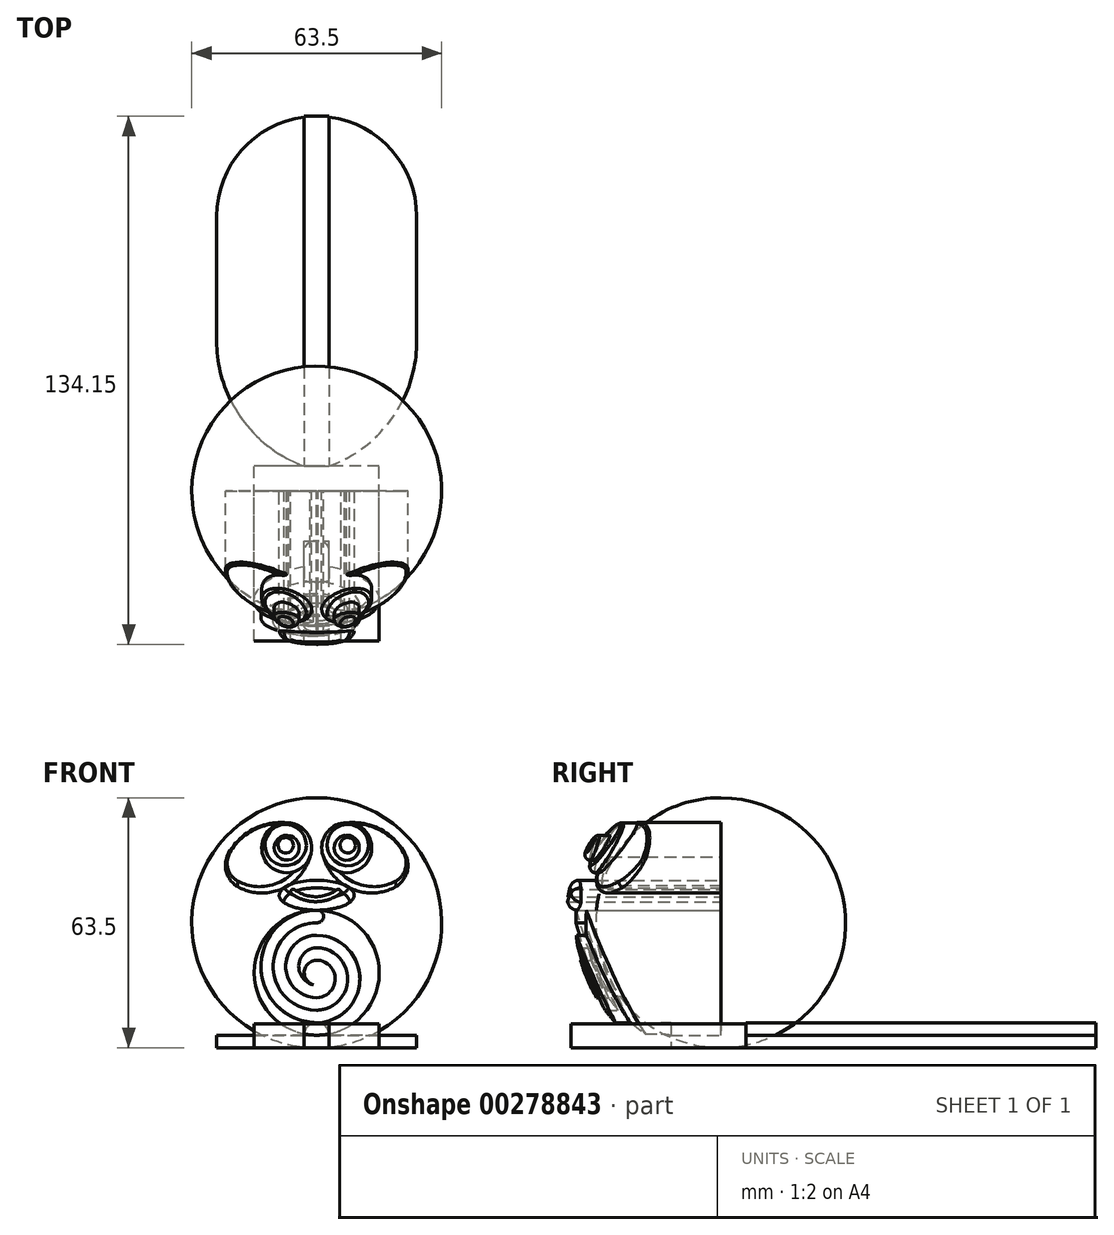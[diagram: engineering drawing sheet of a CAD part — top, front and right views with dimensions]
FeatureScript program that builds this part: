
annotation { "Feature Type Name" : "Feature", "Feature Type Description" : "" }
export const myFeature = defineFeature(function(context is Context, id is Id, definition is map)
    precondition{}
    {
        {
            var Q0;
            Q0=qCreatedBy(makeId("Front.planeOp"),FACE);
            var sketch = newSketch(context, id + "F0", { "sketchPlane" : qUnion([Q0])});
            skArc(sketch, "E0", {"start": v(-7.62, 57.15) * mm, "mid": v(-12.11, 46.3) * mm, "end": v(-1.27, 50.8) * mm});
            skCircle(sketch, "E1", {"center": v(0, 19.05) * mm, "radius": 15.88 * mm});
            skLineSegment(sketch, "E2", {"start": v(-7.62, 50.8) * mm, "end": v(-7.62, 57.15) * mm, "construction": true});
            skArc(sketch, "E3", {"start": v(-7.62, 57.15) * mm, "mid": v(-16.13, 55.5) * mm, "end": v(-22.36, 49.48) * mm});
            skArc(sketch, "E4", {"start": v(-19.75, 40.71) * mm, "mid": v(-7.83, 40.85) * mm, "end": v(-1.27, 50.8) * mm});
            skPoint(sketch, "E5.visualSharp", {"position": v(-24.13, 44.45) * mm});
            skArc(sketch, "E5.filletArc", {"start": v(-22.36, 49.48) * mm, "mid": v(-22.92, 44.54) * mm, "end": v(-19.75, 40.71) * mm});
            skPoint(sketch, "E6.center.orphan", {"position": v(7.62, 50.8) * mm});
            skArc(sketch, "E7.MirrorCS", {"start": v(7.62, 57.15) * mm, "mid": v(12.11, 46.3) * mm, "end": v(1.27, 50.8) * mm});
            skArc(sketch, "E8.MirrorCS", {"start": v(19.75, 40.71) * mm, "mid": v(7.83, 40.85) * mm, "end": v(1.27, 50.8) * mm});
            skArc(sketch, "E9.MirrorCS", {"start": v(22.36, 49.48) * mm, "mid": v(22.92, 44.54) * mm, "end": v(19.75, 40.71) * mm});
            skArc(sketch, "E10.MirrorCS", {"start": v(7.62, 57.15) * mm, "mid": v(16.13, 55.5) * mm, "end": v(22.36, 49.48) * mm});
            skSolve(sketch);
        }
        {
            var Q0;
            Q0 = qSketchRegion(id + "F0", true);
            extrude(context, id + "F1", {"entities" : qUnion([Q0]), "depth" : 50.8 * mm});
        }
        {
            var Q0;
            Q0=qCreatedBy(makeId("Front.planeOp"),FACE);
            var sketch = newSketch(context, id + "F2", { "sketchPlane" : qUnion([Q0])});
            skLineSegment(sketch, "E11", {"start": v(0, 0) * mm, "end": v(0, 63.5) * mm});
            skArc(sketch, "E12", {"start": v(0, 0) * mm, "mid": v(31.75, 31.75) * mm, "end": v(0, 63.5) * mm});
            skSolve(sketch);
        }
        {
            var Q0;
            Q0=qCreatedBy(makeId("Front.planeOp"),FACE);
            var sketch = newSketch(context, id + "F3", { "sketchPlane" : qUnion([Q0])});
            skCircle(sketch, "E13", {"center": v(0, 19.05) * mm, "radius": 12.7 * mm, "construction": true});
            skCircle(sketch, "E14", {"center": v(0, 19.05) * mm, "radius": 15.88 * mm, "construction": true});
            skCircle(sketch, "E15", {"center": v(0, 19.05) * mm, "radius": 9.53 * mm, "construction": true});
            skCircle(sketch, "E16", {"center": v(0, 19.05) * mm, "radius": 6.35 * mm, "construction": true});
            skArc(sketch, "E17", {"start": v(0.3, 22.21) * mm, "mid": v(-3.17, 19.2) * mm, "end": v(0, 15.88) * mm});
            skLineSegment(sketch, "E18", {"start": v(0, 9.53) * mm, "end": v(0, 12.7) * mm, "construction": true});
            skLineSegment(sketch, "E19", {"start": v(15.88, 19.05) * mm, "end": v(-15.88, 19.05) * mm, "construction": true});
            skArc(sketch, "E20", {"start": v(0, 34.92) * mm, "mid": v(-14.19, 20.64) * mm, "end": v(0, 6.35) * mm});
            skLineSegment(sketch, "E21", {"start": v(0, 6.35) * mm, "end": v(0, 3.18) * mm, "construction": true});
            skArc(sketch, "E22", {"start": v(0, 3.17) * mm, "mid": v(14.26, 17.46) * mm, "end": v(0, 31.75) * mm});
            skLineSegment(sketch, "E23.trimOffspring", {"start": v(0, 31.75) * mm, "end": v(0, 34.93) * mm, "construction": true});
            skLineSegment(sketch, "E24.trimOffspring", {"start": v(0, 15.88) * mm, "end": v(0, 22.23) * mm, "construction": true});
            skLineSegment(sketch, "E25.trimOffspring", {"start": v(0, 25.4) * mm, "end": v(0, 28.58) * mm, "construction": true});
            skArc(sketch, "E26", {"start": v(0, 31.75) * mm, "mid": v(-11.08, 20.64) * mm, "end": v(0, 9.53) * mm});
            skArc(sketch, "E27", {"start": v(0, 6.35) * mm, "mid": v(10.96, 17.46) * mm, "end": v(0, 28.58) * mm});
            skArc(sketch, "E28", {"start": v(0, 28.58) * mm, "mid": v(-7.87, 20.64) * mm, "end": v(0, 12.7) * mm});
            skArc(sketch, "E29", {"start": v(0, 9.53) * mm, "mid": v(7.84, 17.46) * mm, "end": v(0, 25.4) * mm});
            skArc(sketch, "E30", {"start": v(0, 12.7) * mm, "mid": v(4.7, 17.46) * mm, "end": v(0, 22.23) * mm});
            skArc(sketch, "E31", {"start": v(0, 25.4) * mm, "mid": v(-4.57, 20.64) * mm, "end": v(0, 15.88) * mm});
            skArc(sketch, "E32", {"start": v(0, 31.75) * mm, "mid": v(1.75, 33.34) * mm, "end": v(0, 34.93) * mm});
            skArc(sketch, "E33", {"start": v(0, 6.35) * mm, "mid": v(-0.24, 6.37) * mm, "end": v(-0.48, 6.36) * mm});
            skArc(sketch, "E34.trimOffspring", {"start": v(-0.6, 3.19) * mm, "mid": v(-0.3, 3.15) * mm, "end": v(0, 3.18) * mm});
            skCircle(sketch, "E35", {"center": v(-7.62, 50.8) * mm, "radius": 6.35 * mm});
            skCircle(sketch, "E36", {"center": v(7.62, 50.8) * mm, "radius": 6.35 * mm});
            skSolve(sketch);
        }
        {
            var Q0;
            Q0=qCreatedBy(makeId("Front.planeOp"),FACE);
            var sketch = newSketch(context, id + "F4", { "sketchPlane" : qUnion([Q0])});
            skLineSegment(sketch, "E37.bottom", {"start": v(-15.88, 0) * mm, "end": v(15.87, 0) * mm});
            skLineSegment(sketch, "E37.top", {"start": v(-15.88, 6.03) * mm, "end": v(15.87, 6.03) * mm});
            skLineSegment(sketch, "E37.left", {"start": v(-15.88, 0) * mm, "end": v(-15.88, 6.03) * mm});
            skLineSegment(sketch, "E37.right", {"start": v(15.87, 0) * mm, "end": v(15.87, 6.03) * mm});
            skSolve(sketch);
        }
        {
            var Q0;
            Q0=qCreatedBy(makeId("Front.planeOp"),FACE);
            var sketch = newSketch(context, id + "F5", { "sketchPlane" : qUnion([Q0])});
            skPoint(sketch, "E38.orphan", {"position": v(0, 4.54) * mm});
            skLineSegment(sketch, "E39", {"start": v(0, 141) * mm, "end": v(0, 66.04) * mm});
            skPoint(sketch, "E40.orphan", {"position": v(0, 72.33) * mm});
            skArc(sketch, "E41", {"start": v(0, -77.5) * mm, "mid": v(109.26, 31.75) * mm, "end": v(0, 141) * mm});
            skArc(sketch, "E42", {"start": v(0, -2.54) * mm, "mid": v(34.3, 31.75) * mm, "end": v(0, 66.04) * mm});
            skLineSegment(sketch, "E43", {"start": v(0, -77.5) * mm, "end": v(0, -2.54) * mm});
            skSolve(sketch);
        }
        {
            var Q0;
            Q0=makeQuery(id+"F5.imprint","IMPRINT",FACE,{"disambiguationData":[TD([[makeQuery(id+"F5.imprint","IMPRINT",EDGE,{"derivedFrom":sQuery(id+"F5.wireOp",EDGE,"E39")}),1.0]])]});
            var Q1;
            Q1=sQuery(id+"F5.wireOp",EDGE,"E39");
            revolve(context, id + "F6", {"operationType" : NewBodyOperationType.REMOVE, "entities" : qUnion([Q0]), "axis" : qUnion([Q1]), "revolveType" : RevolveType.FULL, "oppositeDirection" : true});
        }
        {
            var Q0;
            Q0 = qSketchRegion(id + "F3", true);
            extrude(context, id + "F7", {"entities" : qUnion([Q0]), "operationType" : NewBodyOperationType.ADD, "depth" : 63.5 * mm});
        }
        {
            var Q0;
            Q0=qCreatedBy(makeId("Front.planeOp"),FACE);
            var sketch = newSketch(context, id + "F8", { "sketchPlane" : qUnion([Q0])});
            skArc(sketch, "E44", {"start": v(0, -5.08) * mm, "mid": v(36.83, 31.75) * mm, "end": v(0, 68.58) * mm});
            skArc(sketch, "E45", {"start": v(0, -69.85) * mm, "mid": v(101.6, 31.75) * mm, "end": v(0, 133.35) * mm});
            skLineSegment(sketch, "E46", {"start": v(0, -5.08) * mm, "end": v(0, -69.85) * mm});
            skLineSegment(sketch, "E47", {"start": v(0, 68.58) * mm, "end": v(0, 133.35) * mm});
            skSolve(sketch);
        }
        {
            var Q0;
            Q0 = qSketchRegion(id + "F8", true);
            var Q1;
            Q1=sQuery(id+"F8.wireOp",EDGE,"E47");
            revolve(context, id + "F9", {"operationType" : NewBodyOperationType.REMOVE, "entities" : qUnion([Q0]), "axis" : qUnion([Q1]), "revolveType" : RevolveType.FULL, "oppositeDirection" : true});
        }
        {
            var Q0;
            Q0=qCreatedBy(makeId("Front.planeOp"),FACE);
            var sketch = newSketch(context, id + "F10", { "sketchPlane" : qUnion([Q0])});
            skEllipse(sketch, "E48", {"center": v(0, 38.73) * mm, "majorRadius": 9.53 * mm, "minorRadius": 3.81 * mm, "majorAxis": v(1, 0)});
            skArc(sketch, "E49", {"start": v(-5.61, 40.13) * mm, "mid": v(-0.25, 38.36) * mm, "end": v(5.1, 40.13) * mm});
            skArc(sketch, "E50.0", {"start": v(-6.37, 39.11) * mm, "mid": v(-0.25, 37.1) * mm, "end": v(5.86, 39.11) * mm});
            skArc(sketch, "E51", {"start": v(-5.61, 40.13) * mm, "mid": v(-6.5, 40) * mm, "end": v(-6.37, 39.11) * mm});
            skArc(sketch, "E52", {"start": v(5.86, 39.11) * mm, "mid": v(6, 40) * mm, "end": v(5.1, 40.13) * mm});
            skCircle(sketch, "E53", {"center": v(-7.62, 50.8) * mm, "radius": 3.18 * mm});
            skCircle(sketch, "E54", {"center": v(7.62, 50.8) * mm, "radius": 3.18 * mm});
            skSolve(sketch);
        }
        {
            var Q0;
            Q0 = qSketchRegion(id + "F10", true);
            extrude(context, id + "F11", {"entities" : qUnion([Q0]), "operationType" : NewBodyOperationType.ADD, "depth" : 76.2 * mm});
        }
        {
            var Q0;
            Q0=qCreatedBy(makeId("Front.planeOp"),FACE);
            var sketch = newSketch(context, id + "F12", { "sketchPlane" : qUnion([Q0])});
            skArc(sketch, "E55", {"start": v(0, -7.62) * mm, "mid": v(39.37, 31.75) * mm, "end": v(0, 71.12) * mm});
            skArc(sketch, "E56", {"start": v(0, -69.85) * mm, "mid": v(101.6, 31.75) * mm, "end": v(0, 133.35) * mm});
            skLineSegment(sketch, "E57", {"start": v(0, -7.62) * mm, "end": v(0, -69.85) * mm});
            skLineSegment(sketch, "E58", {"start": v(0, 71.12) * mm, "end": v(0, 133.35) * mm});
            skSolve(sketch);
        }
        {
            var Q0;
            Q0 = qSketchRegion(id + "F12", true);
            var Q1;
            Q1=sQuery(id+"F12.wireOp",EDGE,"E58");
            revolve(context, id + "F13", {"operationType" : NewBodyOperationType.REMOVE, "entities" : qUnion([Q0]), "axis" : qUnion([Q1]), "revolveType" : RevolveType.FULL, "oppositeDirection" : true});
        }
        {
            var Q0;
            Q0 = qSketchRegion(id + "F4", true);
            extrude(context, id + "F14", {"entities" : qUnion([Q0]), "endBound" : BoundingType.SYMMETRIC, "depth" : 76.2 * mm});
        }
        {
            var Q0;
            Q0=makeQuery(id+"F14.opExtrude","SWEPT_FACE",FACE,{"disambiguationData":[OSD([sQuery(id+"F4.wireOp",EDGE,"E37.bottom")])]});
            var sketch = newSketch(context, id + "F15", { "sketchPlane" : qUnion([Q0])});
            skLineSegment(sketch, "E59.bottom", {"start": v(-15.88, -6.35) * mm, "end": v(15.87, -6.35) * mm});
            skLineSegment(sketch, "E59.top", {"start": v(-15.88, -38.1) * mm, "end": v(15.87, -38.1) * mm});
            skLineSegment(sketch, "E59.left", {"start": v(-15.88, -6.35) * mm, "end": v(-15.88, -38.1) * mm});
            skLineSegment(sketch, "E59.right", {"start": v(15.87, -6.35) * mm, "end": v(15.87, -38.1) * mm});
            skLineSegment(sketch, "E60.bottom", {"start": v(-3.18, 38.1) * mm, "end": v(3.17, 38.1) * mm});
            skLineSegment(sketch, "E60.top", {"start": v(-3.17, 12.7) * mm, "end": v(3.18, 12.7) * mm});
            skLineSegment(sketch, "E60.left", {"start": v(-3.18, 38.1) * mm, "end": v(-3.17, 12.7) * mm});
            skLineSegment(sketch, "E60.right", {"start": v(3.17, 38.1) * mm, "end": v(3.18, 12.7) * mm});
            skSolve(sketch);
        }
        {
            var Q0;
            Q0 = qSketchRegion(id + "F15", true);
            extrude(context, id + "F16", {"entities" : qUnion([Q0]), "operationType" : NewBodyOperationType.REMOVE, "oppositeDirection" : true, "depth" : 6.35 * mm});
        }
        {
            var Q0;
            Q0=makeQuery(id+"F14.opExtrude","SWEPT_EDGE",EDGE,{"disambiguationData":[OSD([sQuery(id+"F4.wireOp",EDGE,"E37.top"),sQuery(id+"F4.wireOp",EDGE,"E37.right")])]});
            var Q1;
            {var subQ0=sQuery(id+"F4.wireOp",EDGE,"E37.right");var subQ1=sQuery(id+"F4.wireOp",EDGE,"E37.top");Q1=makeQuery(id+"F16.boolean.opBoolean","SPLIT",EDGE,{"disambiguationData":[TD([makeQuery(id+"F14.opExtrude","SWEPT_FACE",FACE,{"disambiguationData":[OSD([subQ0])]})])],"derivedFrom":makeQuery(id+"F14.opExtrude","CAP_EDGE",EDGE,{"disambiguationData":[OSD([subQ1])],"isStart":false})});}
            var Q2;
            Q2=makeQuery(id+"F14.opExtrude","CAP_EDGE",EDGE,{"disambiguationData":[OSD([sQuery(id+"F4.wireOp",EDGE,"E37.right")])],"isStart":false});
            var Q3;
            Q3=makeQuery(id+"F16.boolean.opBoolean","COPY",EDGE,{"derivedFrom":makeQuery(id+"F16.opExtrude","SWEPT_EDGE",EDGE,{"disambiguationData":[OSD([sQuery(id+"F4.wireOp",EDGE,"E37.bottom"),sQuery(id+"F15.wireOp",EDGE,"E60.bottom"),sQuery(id+"F15.wireOp",EDGE,"E60.right")])]})});
            var Q4;
            Q4=makeQuery(id+"F16.boolean.opBoolean","INTERSECT",EDGE,{"derivedFrom":[makeQuery(id+"F14.opExtrude","SWEPT_FACE",FACE,{"disambiguationData":[OSD([sQuery(id+"F4.wireOp",EDGE,"E37.top")])]}),makeQuery(id+"F16.opExtrude","SWEPT_FACE",FACE,{"disambiguationData":[OSD([sQuery(id+"F15.wireOp",EDGE,"E60.right")])]})]});
            var Q5;
            {var subQ0=sQuery(id+"F4.wireOp",EDGE,"E37.left");var subQ1=sQuery(id+"F4.wireOp",EDGE,"E37.top");Q5=makeQuery(id+"F16.boolean.opBoolean","SPLIT",EDGE,{"disambiguationData":[TD([makeQuery(id+"F14.opExtrude","SWEPT_FACE",FACE,{"disambiguationData":[OSD([subQ0])]})])],"derivedFrom":makeQuery(id+"F14.opExtrude","CAP_EDGE",EDGE,{"disambiguationData":[OSD([subQ1])],"isStart":false})});}
            var Q6;
            Q6=makeQuery(id+"F16.boolean.opBoolean","INTERSECT",EDGE,{"derivedFrom":[makeQuery(id+"F14.opExtrude","SWEPT_FACE",FACE,{"disambiguationData":[OSD([sQuery(id+"F4.wireOp",EDGE,"E37.top")])]}),makeQuery(id+"F16.opExtrude","SWEPT_FACE",FACE,{"disambiguationData":[OSD([sQuery(id+"F15.wireOp",EDGE,"E60.left")])]})]});
            var Q7;
            Q7=makeQuery(id+"F16.boolean.opBoolean","COPY",EDGE,{"derivedFrom":makeQuery(id+"F16.opExtrude","SWEPT_EDGE",EDGE,{"disambiguationData":[OSD([sQuery(id+"F15.wireOp",EDGE,"E60.top"),sQuery(id+"F15.wireOp",EDGE,"E60.left")])]})});
            var Q8;
            Q8=makeQuery(id+"F16.boolean.opBoolean","COPY",EDGE,{"derivedFrom":makeQuery(id+"F16.opExtrude","SWEPT_EDGE",EDGE,{"disambiguationData":[OSD([sQuery(id+"F15.wireOp",EDGE,"E60.top"),sQuery(id+"F15.wireOp",EDGE,"E60.right")])]})});
            var Q9;
            Q9=makeQuery(id+"F14.opExtrude","CAP_EDGE",EDGE,{"disambiguationData":[OSD([sQuery(id+"F4.wireOp",EDGE,"E37.left")])],"isStart":false});
            var Q10;
            Q10=makeQuery(id+"F14.opExtrude","SWEPT_EDGE",EDGE,{"disambiguationData":[OSD([sQuery(id+"F4.wireOp",EDGE,"E37.top"),sQuery(id+"F4.wireOp",EDGE,"E37.left")])]});
            var Q11;
            Q11=makeQuery(id+"F16.boolean.opBoolean","COPY",EDGE,{"derivedFrom":makeQuery(id+"F16.opExtrude","SWEPT_EDGE",EDGE,{"disambiguationData":[OSD([sQuery(id+"F4.wireOp",EDGE,"E37.bottom"),sQuery(id+"F4.wireOp",EDGE,"E37.left"),sQuery(id+"F15.wireOp",EDGE,"E59.bottom"),sQuery(id+"F15.wireOp",EDGE,"E59.left")])]})});
            var Q12;
            Q12=makeQuery(id+"F16.boolean.opBoolean","COPY",EDGE,{"derivedFrom":makeQuery(id+"F16.opExtrude","SWEPT_EDGE",EDGE,{"disambiguationData":[OSD([sQuery(id+"F4.wireOp",EDGE,"E37.bottom"),sQuery(id+"F4.wireOp",EDGE,"E37.right"),sQuery(id+"F15.wireOp",EDGE,"E59.bottom"),sQuery(id+"F15.wireOp",EDGE,"E59.right")])]})});
            fillet(context, id + "F17", {"entities" : qUnion([Q0, Q1, Q2, Q3, Q4, Q5, Q6, Q7, Q8, Q9, Q10, Q11, Q12]), "radius" : 2.54 * mm, "tangentPropagation" : true, "allowEdgeOverflow" : false});
        }
        {
            var Q0;
            Q0=makeQuery(id+"F16.boolean.opBoolean","COPY",FACE,{"derivedFrom":makeQuery(id+"F16.opExtrude","SWEPT_FACE",FACE,{"disambiguationData":[OSD([sQuery(id+"F15.wireOp",EDGE,"E59.bottom")])]})});
            var sketch = newSketch(context, id + "F18", { "sketchPlane" : qUnion([Q0])});
            skLineSegment(sketch, "E61.bottom", {"start": v(-25.4, 0) * mm, "end": v(25.4, 0) * mm});
            skLineSegment(sketch, "E61.top", {"start": v(-25.4, 3.18) * mm, "end": v(-3.18, 3.18) * mm});
            skLineSegment(sketch, "E61.left", {"start": v(-25.4, 0) * mm, "end": v(-25.4, 3.17) * mm});
            skLineSegment(sketch, "E61.right", {"start": v(25.4, 0) * mm, "end": v(25.4, 3.18) * mm});
            skArc(sketch, "E62", {"start": v(3.18, 3.18) * mm, "mid": v(0, 6.35) * mm, "end": v(-3.17, 3.18) * mm});
            skLineSegment(sketch, "E63.trimOffspring", {"start": v(3.17, 3.18) * mm, "end": v(25.4, 3.18) * mm});
            skSolve(sketch);
        }
        {
            var Q0;
            Q0 = qSketchRegion(id + "F18", true);
            extrude(context, id + "F19", {"entities" : qUnion([Q0]), "operationType" : NewBodyOperationType.ADD, "depth" : 88.9 * mm});
        }
        {
            var Q0;
            Q0=makeQuery(id+"F19.opExtrude","SWEPT_FACE",FACE,{"disambiguationData":[OSD([sQuery(id+"F18.wireOp",EDGE,"E63.trimOffspring")])]});
            var sketch = newSketch(context, id + "F20", { "sketchPlane" : qUnion([Q0])});
            skLineSegment(sketch, "E64", {"start": v(-25.4, 38.1) * mm, "end": v(-25.4, 69.85) * mm});
            skLineSegment(sketch, "E65", {"start": v(25.4, 69.85) * mm, "end": v(25.4, 38.1) * mm});
            skArc(sketch, "E66", {"start": v(25.4, 69.85) * mm, "mid": v(0, 95.25) * mm, "end": v(-25.4, 69.85) * mm});
            skArc(sketch, "E67", {"start": v(-25.4, 38.1) * mm, "mid": v(-19.3, 18.72) * mm, "end": v(-3.17, 6.35) * mm});
            skArc(sketch, "E68", {"start": v(3.18, 6.35) * mm, "mid": v(19.3, 18.72) * mm, "end": v(25.4, 38.1) * mm});
            skLineSegment(sketch, "E69", {"start": v(-3.17, 6.35) * mm, "end": v(-41.55, 6.35) * mm});
            skLineSegment(sketch, "E70", {"start": v(-41.55, 6.35) * mm, "end": v(-41.55, 107.73) * mm});
            skLineSegment(sketch, "E71", {"start": v(-41.55, 107.73) * mm, "end": v(64.16, 107.73) * mm});
            skLineSegment(sketch, "E72", {"start": v(64.16, 107.73) * mm, "end": v(64.16, 6.35) * mm});
            skLineSegment(sketch, "E73", {"start": v(64.16, 6.35) * mm, "end": v(3.18, 6.35) * mm});
            skSolve(sketch);
        }
        {
            var Q0;
            Q0 = qSketchRegion(id + "F20", true);
            extrude(context, id + "F21", {"entities" : qUnion([Q0]), "operationType" : NewBodyOperationType.REMOVE, "oppositeDirection" : true, "depth" : 25.4 * mm});
        }
        {
            var Q0;
            Q0 = qSketchRegion(id + "F2", true);
            var Q1;
            Q1=sQuery(id+"F2.wireOp",EDGE,"E11");
            revolve(context, id + "F22", {"entities" : qUnion([Q0]), "axis" : qUnion([Q1]), "revolveType" : RevolveType.FULL});
        }
        {
            var Q0;
            Q0=makeQuery(id+"F13.boolean.opBoolean","INTERSECT",EDGE,{"derivedFrom":[makeQuery(id+"F11.opExtrude","SWEPT_FACE",FACE,{"disambiguationData":[OSD([sQuery(id+"F10.wireOp",EDGE,"E54")])]}),makeQuery(id+"F13.opRevolve","SWEPT_FACE",FACE,{"disambiguationData":[OSD([sQuery(id+"F12.wireOp",EDGE,"E55")])]})]});
            var Q1;
            Q1=makeQuery(id+"F9.boolean.opBoolean","INTERSECT",EDGE,{"derivedFrom":[makeQuery(id+"F7.opExtrude","SWEPT_FACE",FACE,{"disambiguationData":[OSD([sQuery(id+"F3.wireOp",EDGE,"E36")])]}),makeQuery(id+"F9.opRevolve","SWEPT_FACE",FACE,{"disambiguationData":[OSD([sQuery(id+"F8.wireOp",EDGE,"E44")])]})]});
            var Q2;
            Q2=makeQuery(id+"F6.boolean.opBoolean","INTERSECT",EDGE,{"derivedFrom":[makeQuery(id+"F1.opExtrude","SWEPT_FACE",FACE,{"disambiguationData":[OSD([sQuery(id+"F0.wireOp",EDGE,"E10.MirrorCS")])]}),makeQuery(id+"F6.opRevolve","SWEPT_FACE",FACE,{"disambiguationData":[OSD([sQuery(id+"F5.wireOp",EDGE,"E42")])]})]});
            var Q3;
            Q3=makeQuery(id+"F13.boolean.opBoolean","INTERSECT",EDGE,{"derivedFrom":[makeQuery(id+"F11.opExtrude","SWEPT_FACE",FACE,{"disambiguationData":[OSD([sQuery(id+"F10.wireOp",EDGE,"E53")])]}),makeQuery(id+"F13.opRevolve","SWEPT_FACE",FACE,{"disambiguationData":[OSD([sQuery(id+"F12.wireOp",EDGE,"E55")])]})]});
            var Q4;
            {var subQ0=sQuery(id+"F0.wireOp",EDGE,"E4");var subQ1=sQuery(id+"F0.wireOp",EDGE,"E0");Q4=makeQuery(id+"F9.boolean.opBoolean","INTERSECT",EDGE,{"derivedFrom":[makeQuery(id+"F7.boolean.opBoolean","MERGE",FACE,{"derivedFrom":[makeQuery(id+"F1.opExtrude","SWEPT_FACE",FACE,{"disambiguationData":[OSD([subQ1]),TDD([makeQuery(id+"F0.imprint","IMPRINT",EDGE,{"disambiguationData":[TD([[makeQuery(id+"F0.imprint","INTERSECT",VERTEX,{"disambiguationData":[OD(0.0)],"derivedFrom":[subQ1,subQ0]}),1.0]])],"derivedFrom":subQ1})])]}),makeQuery(id+"F7.opExtrude","SWEPT_FACE",FACE,{"disambiguationData":[OSD([sQuery(id+"F3.wireOp",EDGE,"E35")])]})]}),makeQuery(id+"F9.opRevolve","SWEPT_FACE",FACE,{"disambiguationData":[OSD([sQuery(id+"F8.wireOp",EDGE,"E44")])]})]});}
            var Q5;
            {var subQ0=sQuery(id+"F0.wireOp",EDGE,"E4");Q5=makeQuery(id+"F6.boolean.opBoolean","INTERSECT",EDGE,{"derivedFrom":[makeQuery(id+"F1.opExtrude","SWEPT_FACE",FACE,{"disambiguationData":[OSD([subQ0]),TDD([makeQuery(id+"F0.imprint","IMPRINT",EDGE,{"disambiguationData":[TD([[makeQuery(id+"F0.imprint","INTERSECT",VERTEX,{"derivedFrom":[subQ0,sQuery(id+"F0.wireOp",EDGE,"E5.filletArc")]}),-1.0]])],"derivedFrom":subQ0})])]}),makeQuery(id+"F6.opRevolve","SWEPT_FACE",FACE,{"disambiguationData":[OSD([sQuery(id+"F5.wireOp",EDGE,"E42")])]})]});}
            fillet(context, id + "F23", {"entities" : qUnion([Q0, Q1, Q2, Q3, Q4, Q5]), "radius" : 1.27 * mm, "tangentPropagation" : true, "allowEdgeOverflow" : false});
        }
        {
            var Q0;
            Q0=makeQuery(id+"F13.boolean.opBoolean","INTERSECT",EDGE,{"derivedFrom":[makeQuery(id+"F11.opExtrude","SWEPT_FACE",FACE,{"disambiguationData":[OSD([sQuery(id+"F10.wireOp",EDGE,"E48")])]}),makeQuery(id+"F13.opRevolve","SWEPT_FACE",FACE,{"disambiguationData":[OSD([sQuery(id+"F12.wireOp",EDGE,"E55")])]})]});
            fillet(context, id + "F24", {"entities" : qUnion([Q0]), "radius" : 2.54 * mm, "tangentPropagation" : true, "allowEdgeOverflow" : false});
        }
    });
